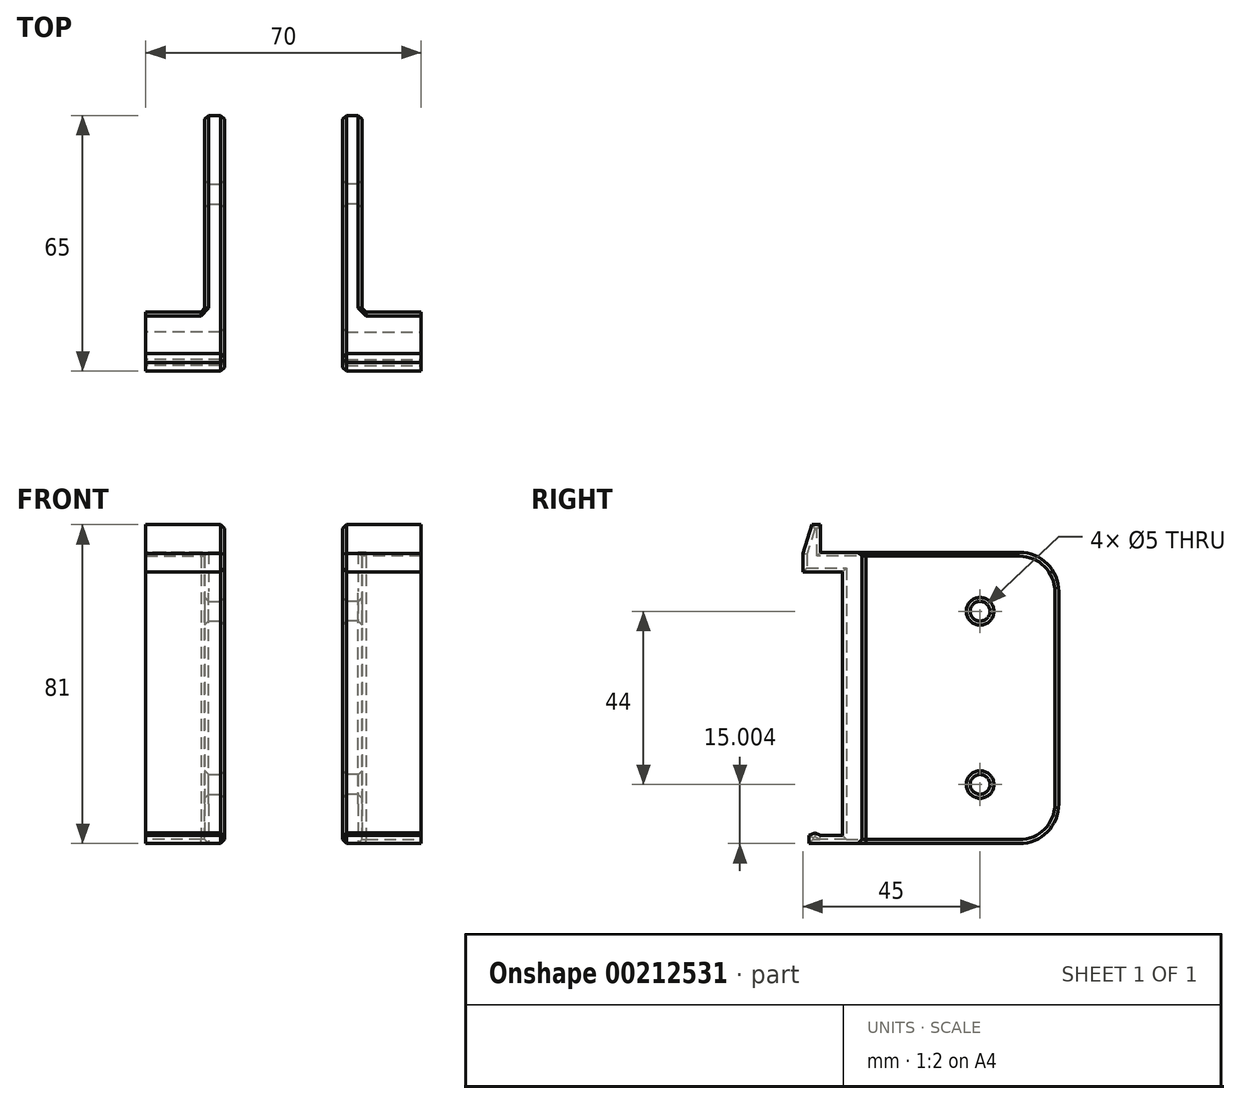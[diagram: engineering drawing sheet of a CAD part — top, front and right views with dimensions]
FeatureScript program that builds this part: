
annotation { "Feature Type Name" : "Feature", "Feature Type Description" : "" }
export const myFeature = defineFeature(function(context is Context, id is Id, definition is map)
    precondition{}
    {
        {
            var Q0;
            Q0=qCreatedBy(makeId("Right.planeOp"),FACE);
            var sketch = newSketch(context, id + "F0", { "sketchPlane" : qUnion([Q0])});
            skLineSegment(sketch, "E0", {"start": v(-23.95, -8.69) * mm, "end": v(-23.95, 58.31) * mm});
            skLineSegment(sketch, "E1", {"start": v(-23.95, 58.31) * mm, "end": v(-33.95, 58.31) * mm});
            skLineSegment(sketch, "E2", {"start": v(-33.95, 58.31) * mm, "end": v(-33.95, 62.98) * mm});
            skLineSegment(sketch, "E3", {"start": v(-31.7, 70.31) * mm, "end": v(-29.45, 70.31) * mm});
            skLineSegment(sketch, "E4", {"start": v(-29.45, 70.31) * mm, "end": v(-29.45, 63.31) * mm});
            skLineSegment(sketch, "E5", {"start": v(-29.45, 63.31) * mm, "end": v(-18.95, 63.31) * mm});
            skLineSegment(sketch, "E6", {"start": v(-18.95, 63.31) * mm, "end": v(-18.95, -10.69) * mm});
            skLineSegment(sketch, "E7", {"start": v(-18.95, -10.69) * mm, "end": v(-32.45, -10.69) * mm});
            skLineSegment(sketch, "E8", {"start": v(-32.45, -10.69) * mm, "end": v(-32.45, -8.69) * mm});
            skLineSegment(sketch, "E9", {"start": v(-29.45, -8.69) * mm, "end": v(-23.95, -8.69) * mm});
            skLineSegment(sketch, "E10", {"start": v(-31.7, 70.31) * mm, "end": v(-33.95, 62.98) * mm});
            skPoint(sketch, "E11.orphan", {"position": v(-33.95, 70.31) * mm});
            skLineSegment(sketch, "E12", {"start": v(-29.45, -8.69) * mm, "end": v(-30.95, -7.94) * mm});
            skLineSegment(sketch, "E13", {"start": v(-30.95, -7.94) * mm, "end": v(-32.45, -8.69) * mm});
            skSolve(sketch);
        }
        {
            var Q0;
            Q0=makeQuery(id+"F0.imprint","IMPRINT",FACE,{"disambiguationData":[TD([[makeQuery(id+"F0.imprint","IMPRINT",EDGE,{"derivedFrom":sQuery(id+"F0.wireOp",EDGE,"E0")}),-1.0]])]});
            extrude(context, id + "F1", {"entities" : qUnion([Q0]), "endBound" : BoundingType.SYMMETRIC, "depth" : 20 * mm});
        }
        {
            var Q0;
            Q0=makeQuery(id+"F1.opExtrude","SWEPT_FACE",FACE,{"disambiguationData":[OSD([sQuery(id+"F0.wireOp",EDGE,"E6")])]});
            var sketch = newSketch(context, id + "F2", { "sketchPlane" : qUnion([Q0])});
            skLineSegment(sketch, "E14", {"start": v(-10, 63.31) * mm, "end": v(-5, 63.31) * mm});
            skLineSegment(sketch, "E15", {"start": v(-5, 63.31) * mm, "end": v(-5, -10.69) * mm});
            skLineSegment(sketch, "E16", {"start": v(-5, -10.69) * mm, "end": v(-10, -10.69) * mm});
            skLineSegment(sketch, "E17", {"start": v(-10, -10.69) * mm, "end": v(-10, 63.31) * mm});
            skSolve(sketch);
        }
        {
            var Q0;
            Q0=makeQuery(id+"F2.imprint","IMPRINT",FACE,{"disambiguationData":[TD([[makeQuery(id+"F2.imprint","IMPRINT",EDGE,{"derivedFrom":sQuery(id+"F2.wireOp",EDGE,"E14")}),-1.0]])]});
            extrude(context, id + "F3", {"entities" : qUnion([Q0]), "operationType" : NewBodyOperationType.ADD, "depth" : 50 * mm});
        }
        {
            var Q0;
            Q0=makeQuery(id+"F3.boolean.opBoolean","MERGE",FACE,{"derivedFrom":[makeQuery(id+"F1.opExtrude","CAP_FACE",FACE,{"disambiguationData":[OSD([sQuery(id+"F0.wireOp",EDGE,"E0"),sQuery(id+"F0.wireOp",EDGE,"E1"),sQuery(id+"F0.wireOp",EDGE,"E2"),sQuery(id+"F0.wireOp",EDGE,"E3"),sQuery(id+"F0.wireOp",EDGE,"E4"),sQuery(id+"F0.wireOp",EDGE,"E5"),sQuery(id+"F0.wireOp",EDGE,"E6"),sQuery(id+"F0.wireOp",EDGE,"E7"),sQuery(id+"F0.wireOp",EDGE,"E8"),sQuery(id+"F0.wireOp",EDGE,"E9"),sQuery(id+"F0.wireOp",EDGE,"E10"),sQuery(id+"F0.wireOp",EDGE,"E12"),sQuery(id+"F0.wireOp",EDGE,"E13")])],"isStart":false}),makeQuery(id+"F3.opExtrude","SWEPT_FACE",FACE,{"disambiguationData":[OSD([sQuery(id+"F2.wireOp",EDGE,"E17")])]})]});
            var sketch = newSketch(context, id + "F4", { "sketchPlane" : qUnion([Q0])});
            skLineSegment(sketch, "E18", {"start": v(31.05, 63.31) * mm, "end": v(11.05, 63.31) * mm, "construction": true});
            skLineSegment(sketch, "E19", {"start": v(11.05, 63.31) * mm, "end": v(11.05, 48.31) * mm, "construction": true});
            skLineSegment(sketch, "E20", {"start": v(31.05, -10.69) * mm, "end": v(11.05, -10.69) * mm, "construction": true});
            skLineSegment(sketch, "E21", {"start": v(11.05, -10.69) * mm, "end": v(11.05, 4.31) * mm, "construction": true});
            skCircle(sketch, "E22", {"center": v(11.05, 48.31) * mm, "radius": 2.5 * mm});
            skCircle(sketch, "E23", {"center": v(11.05, 4.31) * mm, "radius": 2.5 * mm});
            skSolve(sketch);
        }
        {
            var Q0;
            Q0=makeQuery(id+"F4.imprint","IMPRINT",FACE,{"disambiguationData":[TD([[makeQuery(id+"F4.imprint","IMPRINT",EDGE,{"derivedFrom":sQuery(id+"F4.wireOp",EDGE,"E22")}),1.0]])]});
            var Q1;
            Q1=makeQuery(id+"F4.imprint","IMPRINT",FACE,{"disambiguationData":[TD([[makeQuery(id+"F4.imprint","IMPRINT",EDGE,{"derivedFrom":sQuery(id+"F4.wireOp",EDGE,"E23")}),1.0]])]});
            extrude(context, id + "F5", {"entities" : qUnion([Q0, Q1]), "operationType" : NewBodyOperationType.REMOVE, "endBound" : BoundingType.UP_TO_NEXT, "oppositeDirection" : true, "depth" : 25 * mm});
        }
        {
            var Q0;
            Q0=makeQuery(id+"F3.opExtrude","CAP_EDGE",EDGE,{"disambiguationData":[OSD([sQuery(id+"F2.wireOp",EDGE,"E14")])],"isStart":false});
            var Q1;
            Q1=makeQuery(id+"F3.opExtrude","CAP_EDGE",EDGE,{"disambiguationData":[OSD([sQuery(id+"F2.wireOp",EDGE,"E16")])],"isStart":false});
            fillet(context, id + "F6", {"entities" : qUnion([Q0, Q1]), "radius" : 10 * mm, "tangentPropagation" : true, "allowEdgeOverflow" : false});
        }
        {
            var Q0;
            Q0=makeQuery(id+"F3.boolean.opBoolean","MERGE",FACE,{"derivedFrom":[makeQuery(id+"F1.opExtrude","CAP_FACE",FACE,{"disambiguationData":[OSD([sQuery(id+"F0.wireOp",EDGE,"E0"),sQuery(id+"F0.wireOp",EDGE,"E1"),sQuery(id+"F0.wireOp",EDGE,"E2"),sQuery(id+"F0.wireOp",EDGE,"E3"),sQuery(id+"F0.wireOp",EDGE,"E4"),sQuery(id+"F0.wireOp",EDGE,"E5"),sQuery(id+"F0.wireOp",EDGE,"E6"),sQuery(id+"F0.wireOp",EDGE,"E7"),sQuery(id+"F0.wireOp",EDGE,"E8"),sQuery(id+"F0.wireOp",EDGE,"E9"),sQuery(id+"F0.wireOp",EDGE,"E10"),sQuery(id+"F0.wireOp",EDGE,"E12"),sQuery(id+"F0.wireOp",EDGE,"E13")])],"isStart":false}),makeQuery(id+"F3.opExtrude","SWEPT_FACE",FACE,{"disambiguationData":[OSD([sQuery(id+"F2.wireOp",EDGE,"E17")])]})]});
            var Q1;
            Q1=makeQuery(id+"F3.opExtrude","SWEPT_FACE",FACE,{"disambiguationData":[OSD([sQuery(id+"F2.wireOp",EDGE,"E15")])]});
            chamfer(context, id + "F7", {"entities" : qUnion([Q0, Q1]), "width" : 1 * mm, "tangentPropagation" : true});
        }
        {
            var Q0;
            Q0=qCreatedBy(makeId("Right.planeOp"),FACE);
            cPlane(context, id + "F8", {"entities" : qUnion([Q0]), "cplaneType" : CPlaneType.OFFSET, "offset" : 25 * mm, "width" : 150 * mm, "height" : 150 * mm});
        }
        {
            var Q0;
            Q0=makeQuery(id+"F1.opExtrude","SWEPT_BODY",BODY,{"disambiguationData":[OSD([sQuery(id+"F0.wireOp",EDGE,"E0"),sQuery(id+"F0.wireOp",EDGE,"E1"),sQuery(id+"F0.wireOp",EDGE,"E2"),sQuery(id+"F0.wireOp",EDGE,"E3"),sQuery(id+"F0.wireOp",EDGE,"E4"),sQuery(id+"F0.wireOp",EDGE,"E5"),sQuery(id+"F0.wireOp",EDGE,"E6"),sQuery(id+"F0.wireOp",EDGE,"E7"),sQuery(id+"F0.wireOp",EDGE,"E8"),sQuery(id+"F0.wireOp",EDGE,"E9"),sQuery(id+"F0.wireOp",EDGE,"E10"),sQuery(id+"F0.wireOp",EDGE,"E12"),sQuery(id+"F0.wireOp",EDGE,"E13")])]});
            var Q1;
            Q1=qCreatedBy(id+"F8.planeOp",FACE);
            mirror(context, id + "F9", {"entities" : qUnion([Q0]), "mirrorPlane" : qUnion([Q1])});
        }
    });
